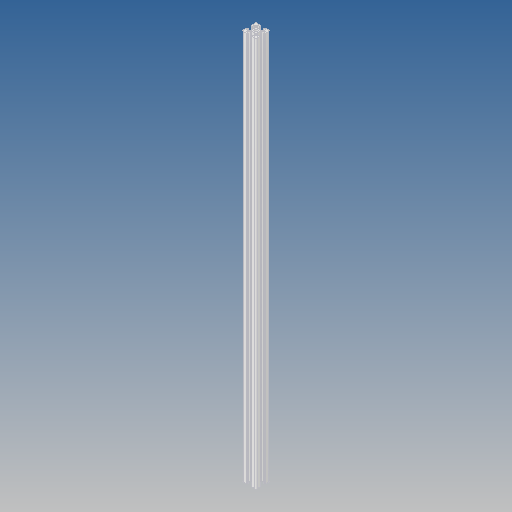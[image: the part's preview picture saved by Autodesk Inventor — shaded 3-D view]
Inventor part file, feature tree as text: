
AUTODESK INVENTOR PART (.ipt)
format: ipt  version: 2018 (Build 220112000, 112)  size: 247,296 bytes
history: native  units: mm
features: other x1, extrude x1, sketch x1, projected_geometry x1
ambient origin geometry x8: Origin, YZ Plane, XZ Plane, XY Plane, X Axis, Y Axis, Z Axis, Center Point
bodies: Solid1 (feature_tree), Body1 (feature_tree)
feature tree (4):
  other  "<userpath>\OneDrive\Objet3D\3DPrinter\Parameters.xlsx"
  extrude  "Extrusion1"  [1 undecoded]
  sketch  "Sketch1"  dims[d0=460.0mm d1=0.0mm]
  projected_geometry  "Projected Loop1"
note: 1 required parameter value undecoded (feature->parameter linkage not recoverable at this tier; creation-order binding heuristic only, values carry confidence <= 0.55)
